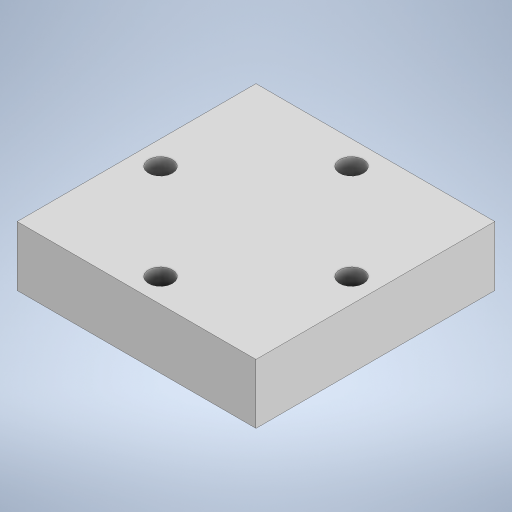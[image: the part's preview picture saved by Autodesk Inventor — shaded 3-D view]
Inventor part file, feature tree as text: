
AUTODESK INVENTOR PART (.ipt)
format: ipt  version: 2024 (Build 280153000, 153)  size: 209,920 bytes
history: native  units: in
note: dims shown in document units (in); Inventor stores cm internally (conversion verified against a paired STEP export)
features: extrude x2, sketch x2
ambient origin geometry x8: Origin, YZ Plane, XZ Plane, XY Plane, X Axis, Y Axis, Z Axis, Center Point
bodies: Solid1 (feature_tree)
feature tree (4):
  extrude  "Extrusion1"  Depth=0.625in TaperAngle=0.0deg
  extrude  "Extrusion2"  TaperAngle=0.0deg  [1 undecoded]
  sketch  "Sketch1"  dims[d0=2.5in d1=0.625in d2=0.0in]
  sketch  "Sketch2"  dims[d3=0.25in d6=0.0in d7=1.0in d8=1.5748in d10=360.0deg d12=2.0in d13=0.0in]
note: 1 required parameter value undecoded (feature->parameter linkage not recoverable at this tier; creation-order binding heuristic only, values carry confidence <= 0.55)
